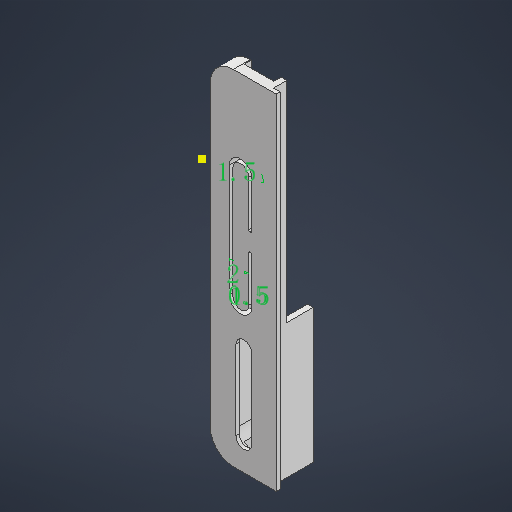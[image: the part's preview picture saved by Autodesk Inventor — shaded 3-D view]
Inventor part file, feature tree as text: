
AUTODESK INVENTOR PART (.ipt)
format: ipt  version: 2025 (Build 290162000, 162)  size: 474,624 bytes
history: native  units: mm
features: extrude x12, reference x12, sketch x11, other x11, projected_geometry x6, fillet x3, plane x1
ambient origin geometry x8: Origin, YZ Plane, XZ Plane, XY Plane, X Axis, Y Axis, Z Axis, Center Point
bodies: 实体1 (feature_tree)
feature tree (56):
  extrude  "拉伸1"  Depth=10.0mm TaperAngle=0.0deg
  sketch  "草图2"  dims[d4=10.0mm d5=0.0mm d6=0.2mm]
  plane  "工作平面1"
  extrude  "拉伸2"  Depth=10.0mm
  extrude  "拉伸3"  Depth=0.4mm TaperAngle=0.0deg
  extrude  "拉伸4"  Depth=3.4mm
  sketch  "草图5"  dims[d14=1.0mm d15=3.9mm d16=0.0mm]
  extrude  "拉伸5"  Depth=3.9mm TaperAngle=0.0deg
  extrude  "拉伸6"  Depth=4.5mm
  extrude  "拉伸7"  Depth=1.5mm TaperAngle=0.0deg
  fillet  "圆角1"  Radius=0.2mm
  fillet  "圆角2"  Radius=1.0mm
  extrude  "拉伸8"  Depth=1.1mm TaperAngle=0.0deg
  fillet  "圆角3"  Radius=0.2mm
  extrude  "拉伸10"  Depth=1.1mm TaperAngle=0.0deg
  other  "直接编辑1"
  extrude  "拉伸11"  Depth=1.5mm
  extrude  "拉伸12"  Depth=4.0mm TaperAngle=0.0deg
  other  "直接编辑2"
  extrude  "拉伸13"  Depth=15.0mm TaperAngle=0.0deg
  sketch  "草图1"  dims[d0=3.0mm d1=0.0mm d2=10.0mm d3=0.0mm]
  reference  "参考1"
  reference  "参考2"
  reference  "参考3"
  reference  "参考4"
  reference  "参考5"
  reference  "参考6"
  sketch  "草图3"  dims[d7=0.2mm d8=0.4mm d9=0.0mm]
  reference  "参考8"
  reference  "参考9"
  sketch  "草图4"  dims[d11=20.4mm d13=3.4mm]
  projected_geometry  "投影回路1"
  sketch  "草图8"  dims[d18=0.5mm d19=0.0mm d20=4.5mm]
  reference  "参考11"
  reference  "参考12"
  projected_geometry  "投影回路2"
  sketch  "草图11"  dims[d21=4.5mm d22=1.5mm d23=0.0mm d24=0.2mm d25=1.0mm]
  sketch  "草图12"  dims[d26=1.5mm d27=1.1mm d28=0.0mm d29=0.2mm]
  reference  "参考13"
  reference  "参考14"
  sketch  "草图13"  dims[d33=2.0mm d35=1.1mm d36=0.0mm]
  projected_geometry  "投影回路3"
  projected_geometry  "投影回路4"
  projected_geometry  "投影回路5"
  sketch  "草图14"  dims[d37=0.0mm d38=0.0mm d39=-0.5mm d41=1.5mm]
  projected_geometry  "投影回路6"
  sketch  "草图15"  dims[d42=0.5mm d43=4.0mm d44=0.0mm d45=15.0mm d46=0.0mm d47=2.0mm d48=6.0mm d49=0.0mm d50=0.5mm d51=0.872665mm d52=0.5mm d53=0.872665mm]
  parser-record x2  (decoder bookkeeping rows leaked as tree rows — omitted from the tree; the rows remain in map.json)
  other  "装配体.iam"
  other  "键盘外壳:1"
  other  "dlc.iam"
  other  "指纹识别:1"
  other  "音量接口:1"
  other  "移动1"
  other  "删除1"
note: 2 file-system paths scrubbed to <path> (originals preserved in map.json)
